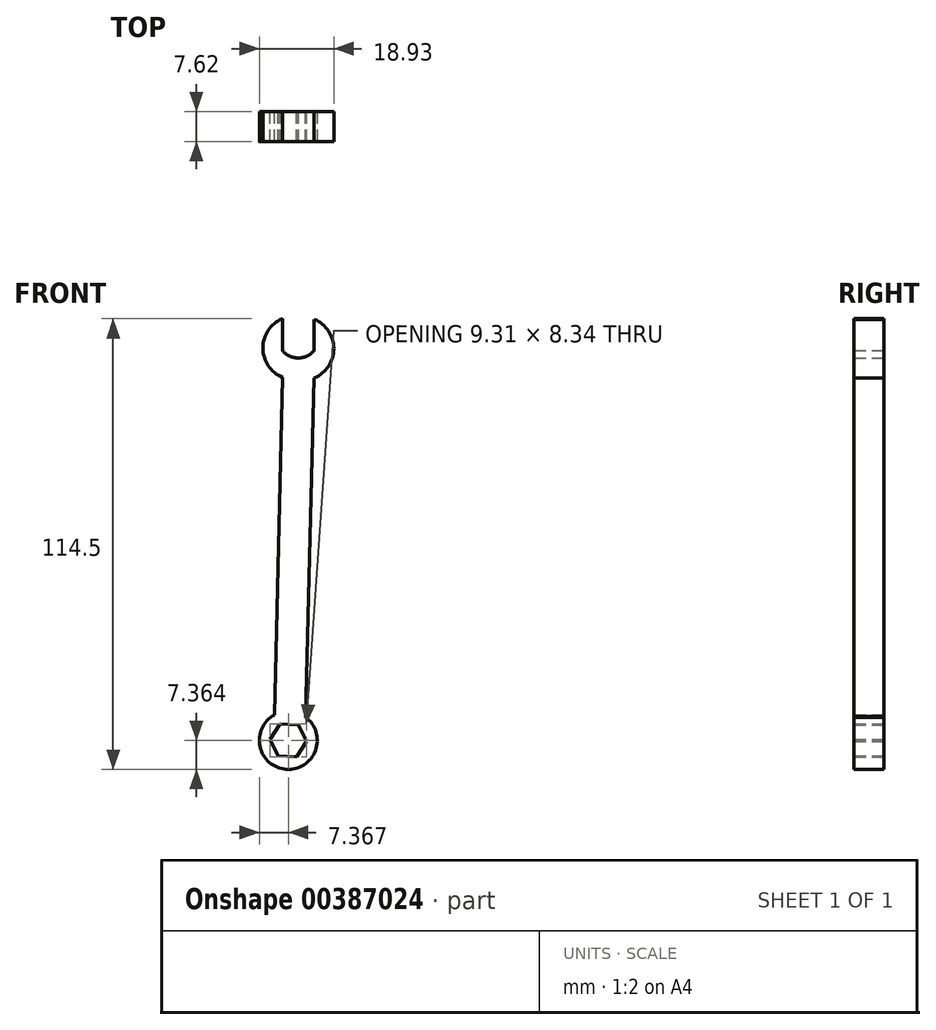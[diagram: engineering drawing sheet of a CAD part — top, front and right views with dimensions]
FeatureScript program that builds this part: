
annotation { "Feature Type Name" : "Feature", "Feature Type Description" : "" }
export const myFeature = defineFeature(function(context is Context, id is Id, definition is map)
    precondition{}
    {
        {
            var Q0;
            Q0=qCreatedBy(makeId("Front.planeOp"),FACE);
            var sketch = newSketch(context, id + "F0", { "sketchPlane" : qUnion([Q0])});
            skLineSegment(sketch, "E0.3", {"start": v(-48.42, -94.85) * mm, "end": v(-55.2, -90.71) * mm});
            skPoint(sketch, "E0.0.midPoint", {"position": v(-31.44, -87.87) * mm});
            skLineSegment(sketch, "E1", {"start": v(-39.74, -65.43) * mm, "end": v(-37.6, 20.52) * mm});
            skLineSegment(sketch, "E2", {"start": v(-37.6, 20.52) * mm, "end": v(-45.67, 20.72) * mm});
            skLineSegment(sketch, "E3", {"start": v(-45.67, 20.72) * mm, "end": v(-47.68, -65.24) * mm});
            skArc(sketch, "E4", {"start": v(-37.6, 20.52) * mm, "mid": v(-32.6, 27.98) * mm, "end": v(-37.6, 35.45) * mm});
            skLineSegment(sketch, "E5", {"start": v(-45.68, 27.53) * mm, "end": v(-45.68, 35.6) * mm});
            skArc(sketch, "E6", {"start": v(-45.68, 35.6) * mm, "mid": v(-50.61, 28.16) * mm, "end": v(-45.67, 20.72) * mm});
            skCircle(sketch, "E7.cCircle", {"center": v(-44.16, -71.54) * mm, "radius": 4.04 * mm, "construction": true});
            skLineSegment(sketch, "E7.0", {"start": v(-41.6, -67.64) * mm, "end": v(-39.5, -71.82) * mm});
            skLineSegment(sketch, "E7.1", {"start": v(-39.5, -71.82) * mm, "end": v(-42.08, -75.7) * mm});
            skLineSegment(sketch, "E7.2", {"start": v(-42.08, -75.7) * mm, "end": v(-46.73, -75.43) * mm});
            skLineSegment(sketch, "E7.3", {"start": v(-46.73, -75.43) * mm, "end": v(-48.82, -71.26) * mm});
            skLineSegment(sketch, "E7.4", {"start": v(-48.82, -71.26) * mm, "end": v(-46.25, -67.36) * mm});
            skLineSegment(sketch, "E7.5", {"start": v(-46.25, -67.36) * mm, "end": v(-41.6, -67.64) * mm});
            skPoint(sketch, "E7.0.midPoint", {"position": v(-40.55, -69.73) * mm});
            skCircle(sketch, "E8", {"center": v(-44.16, -71.54) * mm, "radius": 7.37 * mm});
            skLineSegment(sketch, "E9", {"start": v(-37.6, 35.45) * mm, "end": v(-37.6, 27.53) * mm});
            skArc(sketch, "E10", {"start": v(-45.68, 27.53) * mm, "mid": v(-41.64, 25.62) * mm, "end": v(-37.6, 27.53) * mm});
            skLineSegment(sketch, "E11", {"start": v(-39.74, -65.43) * mm, "end": v(-39.74, -66.02) * mm});
            skSolve(sketch);
        }
        {
            var Q0;
            {var subQ6=sQuery(id+"F0.wireOp",EDGE,"E1");Q0=makeQuery(id+"F0.imprint","IMPRINT",FACE,{"disambiguationData":[TD([[makeQuery(id+"F0.imprint","IMPRINT",EDGE,{"derivedFrom":subQ6}),1.0]])]});}
            extrude(context, id + "F1", {"entities" : qUnion([Q0]), "depth" : 6.35 * mm});
        }
        {
            var Q0;
            Q0 = qSketchRegion(id + "F0", true);
            extrude(context, id + "F2", {"entities" : qUnion([Q0]), "operationType" : NewBodyOperationType.ADD, "depth" : 7.62 * mm});
        }
    });
